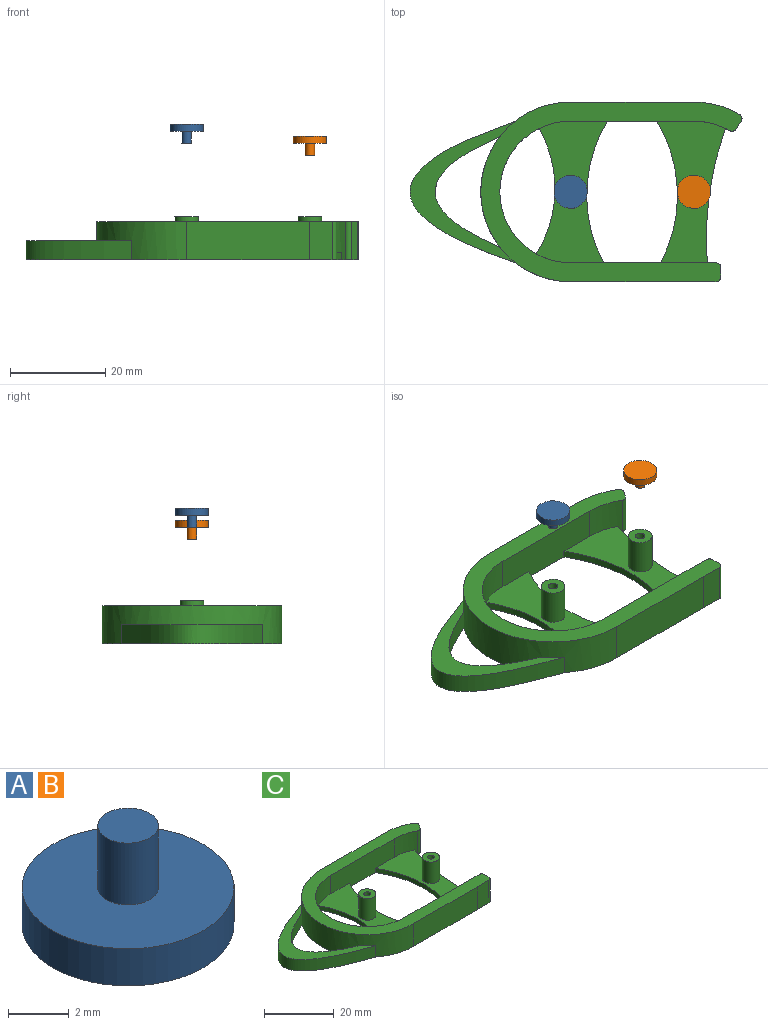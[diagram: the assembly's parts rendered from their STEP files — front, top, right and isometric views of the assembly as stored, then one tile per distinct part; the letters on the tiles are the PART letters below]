
ASSEMBLY  parts=3 mates=2
PART A: 5 faces, bbox 7x7x4 mm
  f0: cylinder r=1mm len=2.5mm, axis (0,0,-1), area 15.7mm2, adj f1,f3
  f1: plane 2x2mm, normal (0,0,1), area 3.1mm2, adj f0
  f2: cylinder r=3.5mm len=7mm, axis (0,0,-1), area 33mm2, adj f3,f4
  f3: plane 7x7mm, normal (0,0,1), area 35.3mm2, adj f0,f2
  f4: plane 7x7mm, normal (0,0,-1), area 38.5mm2, adj f2
PART B: same geometry as A
PART C: 35 faces, bbox 78.1x37.8x9 mm
  f0: plane 25.83x8mm, normal (0,-1,0), area 183.5mm2, adj f7,f8,f12,f13,f17,f19,f21,f22
  f1: cylinder r=18.9mm len=37.8mm, axis (0,0,-1), area 437.9mm2, adj f2,f11,f12,f13,f14,f15,f16
  f2: plane 25.82x8mm, normal (0,-1,0), area 206.6mm2, adj f1,f3,f12,f13
  f3: plane 8x4.75mm, normal (-0.01,-1,0), area 38mm2, adj f2,f12,f13,f27
  f4: plane 8x2mm, normal (1,-0.01,0), area 16mm2, adj f12,f13,f27,f28
  f5: plane 8x4.76mm, normal (0.01,1,0), area 33.8mm2, adj f6,f12,f13,f18,f19,f28
  f6: plane 25.83x8mm, normal (0,1,0), area 185.9mm2, adj f5,f7,f12,f13,f17,f19,f21,f22
  f7: cylinder r=14.9mm len=29.8mm, axis (0,0,-1), area 352.9mm2, adj f0,f6,f12,f13,f20,f22
  f8: cylinder r=14.9mm len=8mm, axis (0,0,-1), area 53.1mm2, adj f0,f12,f13,f18,f19,f29
  f9: plane 8x1.66mm, normal (0.83,-0.56,0), area 16mm2, adj f12,f13,f29,f30
  f10: cylinder r=18.9mm len=9.72mm, axis (0,0,-1), area 81.6mm2, adj f11,f12,f13,f30
  f11: plane 25.82x8mm, normal (0,1,0), area 206.6mm2, adj f1,f10,f12,f13
  f12: plane 54.94x37.83mm, normal (0,0,1), area 481.4mm2, adj f0,f1,f2,f3,f4,f5,f6,f7
  f13: plane 78.13x37.83mm, normal (0,0,-1), area 1148.1mm2, adj f0,f1,f2,f3,f4,f5,f6,f7
  f14: extruded ~29.8x22.16mm, area 223.3mm2, adj f1,f13,f16
  f15: extruded ~23.26x13.59mm, area 149.8mm2, adj f1,f13,f16
  f16: plane 30.47x29.8mm, normal (0,0,1), area 141.9mm2, adj f1,f14,f15
  f17: cylinder r=30.23mm len=29.8mm, axis (0,0,-1), area 46.8mm2, adj f0,f6,f13,f19
  f18: cylinder r=67.29mm len=28.26mm, axis (0,0,-1), area 43.1mm2, adj f5,f8,f13,f19
  f19: plane 29.82x14.42mm, normal (0,0,1), area 232.6mm2, adj f0,f5,f6,f8,f17,f18,f25
  f20: cylinder r=25.86mm len=26.39mm, axis (0,0,-1), area 41.5mm2, adj f7,f13,f22
  f21: cylinder r=30.23mm len=29.8mm, axis (0,0,-1), area 46.8mm2, adj f0,f6,f13,f22
  f22: plane 29.8x14.92mm, normal (0,0,1), area 252.9mm2, adj f0,f6,f7,f20,f21,f23
  f23: cylinder r=2.5mm len=7.5mm, axis (0,0,-1), area 117.8mm2, adj f22,f24
  f24: plane 5x5mm, normal (0,0,1), area 16.5mm2, adj f23,f31
  f25: cylinder r=2.5mm len=7.5mm, axis (0,0,-1), area 117.8mm2, adj f19,f26
  f26: plane 5x5mm, normal (0,0,1), area 16.5mm2, adj f25,f33
  f27: cylinder r=1mm len=8mm, axis (0,0,1), area 12.6mm2, adj f3,f4,f12,f13
  f28: cylinder r=1mm len=8mm, axis (0,0,-1), area 12.6mm2, adj f4,f5,f12,f13
  f29: cylinder r=1mm len=8mm, axis (0,0,-1), area 12.1mm2, adj f8,f9,f12,f13
  f30: cylinder r=1mm len=8mm, axis (0,0,-1), area 13mm2, adj f9,f10,f12,f13
  f31: cylinder r=1mm len=5mm, axis (0,0,1), area 31.4mm2, adj f24,f32
  f32: plane 2x2mm, normal (0,0,1), area 3.1mm2, adj f31
  f33: cylinder r=1mm len=5mm, axis (0,0,1), area 31.4mm2, adj f26,f34
  f34: plane 2x2mm, normal (0,0,1), area 3.1mm2, adj f33
PLACE A rot(axis=(1,0,0),180deg) t=(-28.47,4.95,16.7)mm
PLACE B rot(axis=(1,0,0),180deg) t=(-2.55,4.95,14.17)mm
PLACE C t=(-15.55,4.95,-11.8)mm
MATE slider B.f0 <-> C.f33  axis (0,0,-1) through (-2.55,4.95,10.17)mm
MATE slider A.f0 <-> C.f23  axis (0,0,-1) through (-28.47,4.95,12.7)mm
